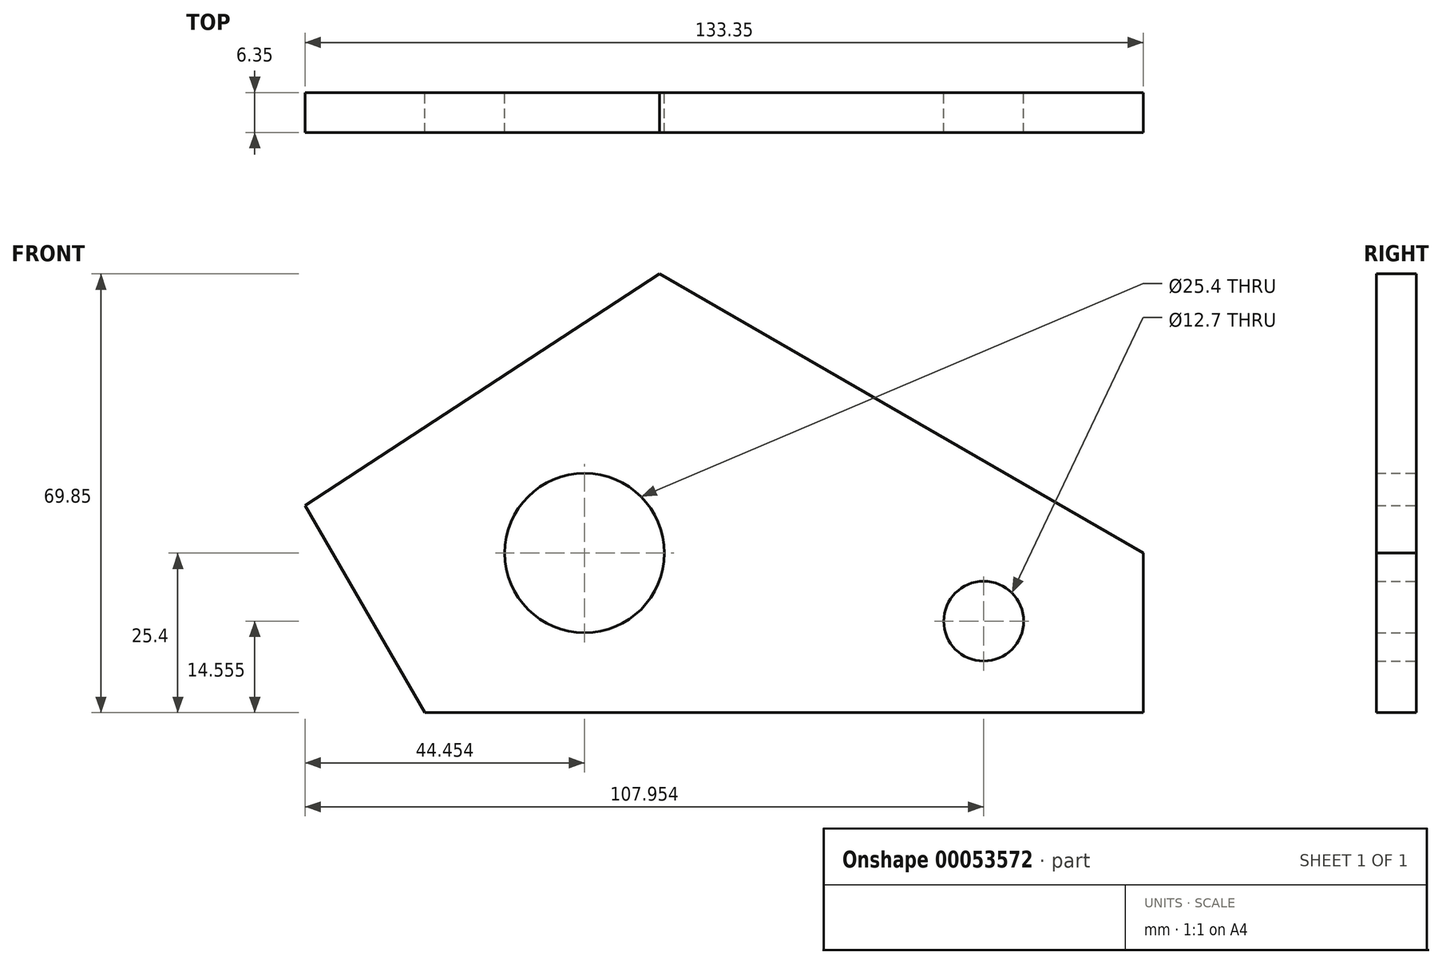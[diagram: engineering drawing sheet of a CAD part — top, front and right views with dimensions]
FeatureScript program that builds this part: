
annotation { "Feature Type Name" : "Feature", "Feature Type Description" : "" }
export const myFeature = defineFeature(function(context is Context, id is Id, definition is map)
    precondition{}
    {
        {
            var Q0;
            Q0=qCreatedBy(makeId("Front.planeOp"),FACE);
            var sketch = newSketch(context, id + "F0", { "sketchPlane" : qUnion([Q0])});
            skLineSegment(sketch, "E0", {"start": v(-57, -34.3) * mm, "end": v(57.3, -34.3) * mm});
            skLineSegment(sketch, "E1", {"start": v(57.3, -34.3) * mm, "end": v(57.3, -8.9) * mm});
            skLineSegment(sketch, "E2", {"start": v(57.3, -8.9) * mm, "end": v(-19.7, 35.55) * mm});
            skLineSegment(sketch, "E3", {"start": v(-19.7, 35.55) * mm, "end": v(-76.06, -1.3) * mm});
            skLineSegment(sketch, "E4", {"start": v(-76.06, -1.3) * mm, "end": v(-57, -34.3) * mm});
            skCircle(sketch, "E5", {"center": v(-31.6, -8.9) * mm, "radius": 12.7 * mm});
            skCircle(sketch, "E6", {"center": v(31.9, -19.75) * mm, "radius": 6.35 * mm});
            skSolve(sketch);
        }
        {
            var Q0;
            Q0 = qSketchRegion(id + "F0", true);
            extrude(context, id + "F1", {"entities" : qUnion([Q0]), "depth" : 6.35 * mm});
        }
    });
